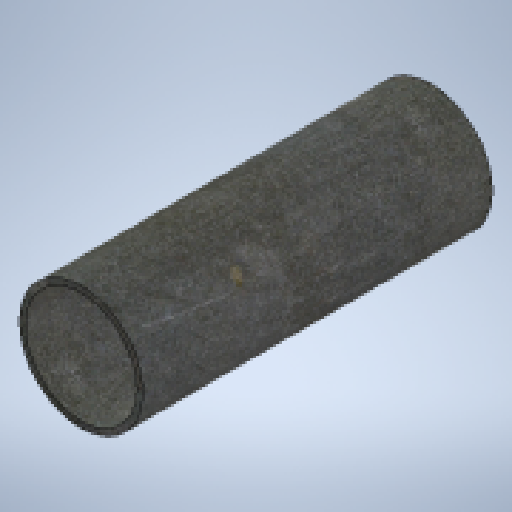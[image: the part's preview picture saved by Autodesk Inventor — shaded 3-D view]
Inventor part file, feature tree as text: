
AUTODESK INVENTOR PART (.ipt)
format: ipt  version: 2025.1 (Build 291241020, 241B)  size: 161,792 bytes
history: native  units: mm
features: extrude x1, sketch x1
ambient origin geometry x8: Origin, YZ Plane, XZ Plane, XY Plane, X Axis, Y Axis, Z Axis, Center Point
bodies: Solid1 (feature_tree)
feature tree (2):
  extrude  "Extrusion1"  Depth=120.0mm
  sketch  "Sketch1"  dims[d0=60.0mm d1=3.0mm d2=120.0mm d3=0.0mm]
